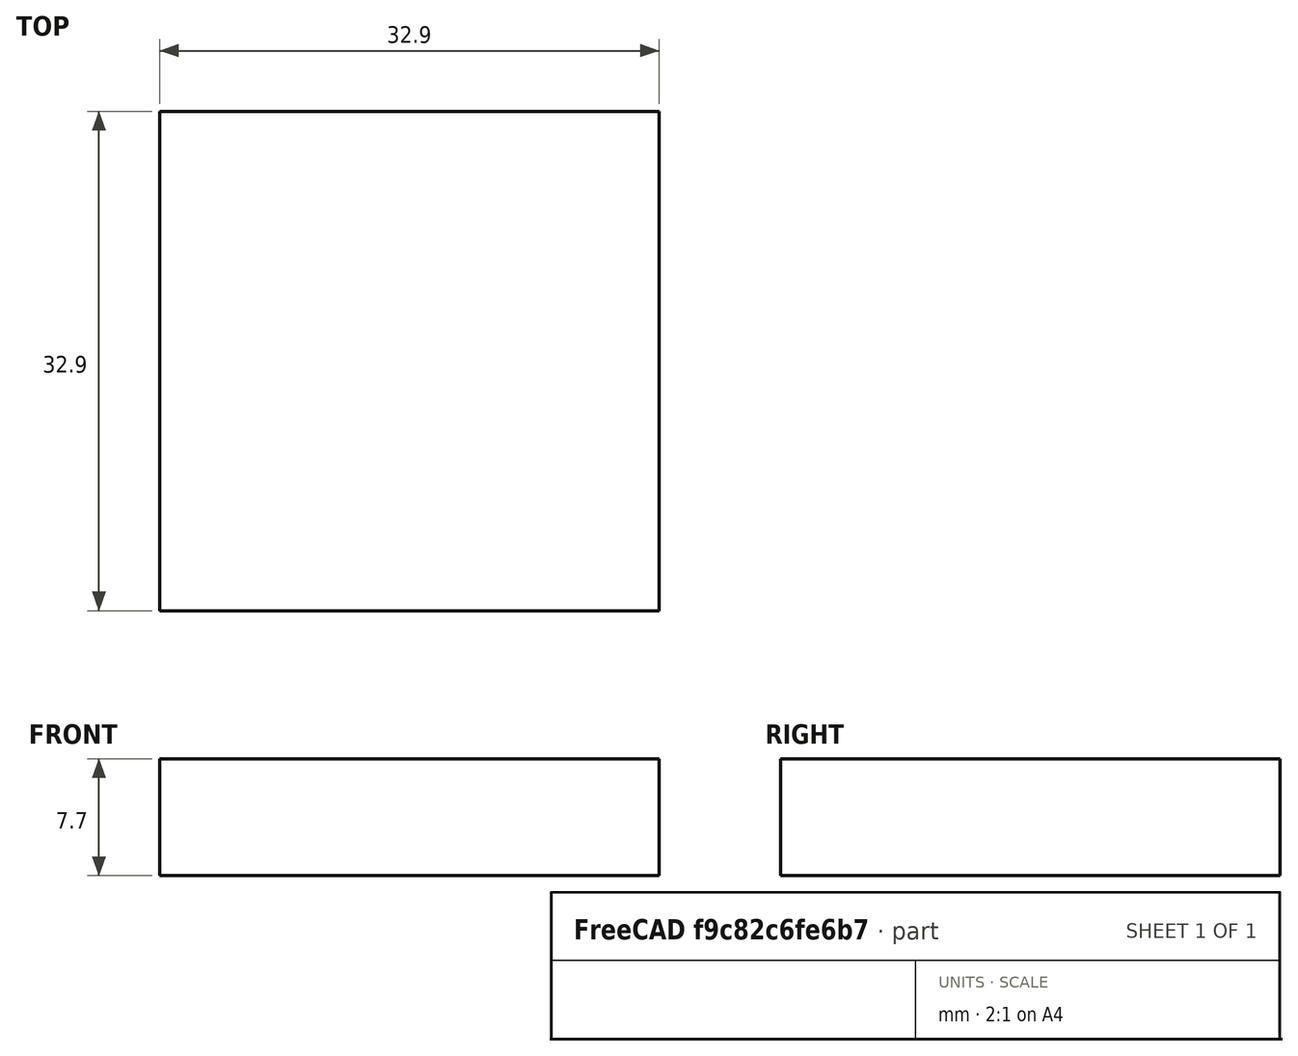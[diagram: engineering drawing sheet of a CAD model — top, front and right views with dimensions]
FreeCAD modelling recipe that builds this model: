
FCSTD DOCUMENT  (FreeCAD 0.18.4R)
Label: midi_pad
License: All rights reserved
LicenseURL: http://en.wikipedia.org/wiki/All_rights_reserved
objects: Path::FeaturePython×5, App::MeasureDistance×4, Sketcher::SketchObject×3, PartDesign::Pocket×2, Part::FeaturePython×2, PartDesign::Pad×1, Spreadsheet::Sheet×1, PartDesign::Body×1, App::FeaturePython×1, App::DocumentObjectGroup×1, Path::FeatureCompoundPython×1, Mesh::FeaturePython×1, Image::ImagePlane×1
note: 14 computed .brp shape members not serialized (recipe doc carries the construction recipe); baked Part::Feature solids carry a one-line shape summary decoded from their .brp

FEATURE [Sketcher::SketchObject] Sketch  label="circle"
  MapMode = 5
  Support = -> [XY_Plane]
  expr: Constraints[1] = parameters.balero_R + parameters.wall_thickness * 2
  sketch-geometry (1):
    g0: Circle CenterX=0 CenterY=0 CenterZ=0 NormalX=0 NormalY=0 NormalZ=1 AngleXU=0 Radius=11.45
  constraints (2):
    c: Coincident(g0,g-1)
    c: Diameter(g0) = 22.9
FEATURE [PartDesign::Pad] Pad  label="cilinder"
  Length = 7.7
  Length2 = 100
  Profile = -> Sketch
  Type = 0
  expr: Length = parameters.balero_h + parameters.cutout_d + parameters.separator
FEATURE [Sketcher::SketchObject] Sketch002  label="cutout"
  MapMode = 5
  Placement = pos=(0,0,0) rot=(1,0,0;3.14159rad)
  expr: Constraints[34] = (parameters.balero_R + parameters.wall_thickness) / 2
  expr: Constraints[33] = (parameters.balero_R + parameters.wall_thickness) / 2
  expr: Constraints[32] = (parameters.balero_R + parameters.wall_thickness) / 2
  expr: Constraints[35] = (parameters.balero_R + parameters.wall_thickness) / 2
  expr: Constraints.pin_width = parameters.pin_w
  expr: Constraints[13] = parameters.r_w
  sketch-geometry (12):
    g0: LineSegment StartX=-9.7 StartY=5.1 StartZ=0 EndX=-5 EndY=5.1 EndZ=0
    g1: LineSegment StartX=-5 StartY=5.1 StartZ=0 EndX=-5 EndY=9.7 EndZ=0
    g2: LineSegment StartX=-5 StartY=9.7 StartZ=0 EndX=5 EndY=9.7 EndZ=0
    g3: LineSegment StartX=5 StartY=9.7 StartZ=0 EndX=5 EndY=5.1 EndZ=0
    g4: LineSegment StartX=5 StartY=5.1 StartZ=0 EndX=9.7 EndY=5.1 EndZ=0
    g5: LineSegment StartX=9.7 StartY=5.1 StartZ=0 EndX=9.7 EndY=-5.1 EndZ=0
    g6: LineSegment StartX=9.7 StartY=-5.1 StartZ=0 EndX=5 EndY=-5.1 EndZ=0
    g7: LineSegment StartX=5 StartY=-5.1 StartZ=0 EndX=5 EndY=-9.7 EndZ=0
    g8: LineSegment StartX=5 StartY=-9.7 StartZ=0 EndX=-5 EndY=-9.7 EndZ=0
    g9: LineSegment StartX=-5 StartY=-9.7 StartZ=0 EndX=-5 EndY=-5.1 EndZ=0
    g10: LineSegment StartX=-5 StartY=-5.1 StartZ=0 EndX=-9.7 EndY=-5.1 EndZ=0
    g11: LineSegment StartX=-9.7 StartY=-5.1 StartZ=0 EndX=-9.7 EndY=5.1 EndZ=0
  constraints (36):
    c: Horizontal(g0)
    c: Coincident(g0,g1)
    c: Coincident(g1,g2)
    c: Coincident(g2,g3)
    c: Coincident(g3,g4)
    c: Coincident(g4,g5)
    c: Coincident(g5,g6)
    c: Coincident(g6,g7)
    c: Coincident(g7,g8)
    c: Coincident(g8,g9)
    c: Coincident(g9,g10)
    c: Coincident(g10,g11)
    c: Coincident(g11,g0)
    c: DistanceX(g2,g2) = 10
    c: Equal(g2,g8)
    c: Vertical(g1)
    c: Vertical(g3)
    c: Vertical(g5)
    c: Vertical(g11)
    c: Vertical(g9)
    c: Horizontal(g2)
    c: Horizontal(g4)
    c: Horizontal(g6)
    c: Horizontal(g8)
    c: DistanceY(g5,g5) = 10.2  'pin_width'
    c: Equal(g5,g11)
    c: Equal(g1,g3)
    c: Equal(g4,g6)
    c: Equal(g9,g7)
    c: Equal(g10,g0)
    c: Equal(g0,g4)
    c: Equal(g9,g1)
    c: DistanceX(g-1,g4) = 9.7
    c: DistanceX(g0,g-1) = 9.7
    c: DistanceY(g-1,g1) = 9.7
    c: DistanceY(g8,g-1) = 9.7
FEATURE [Spreadsheet::Sheet] Spreadsheet  label="parameters"
  cells = A1=balero_R; B1(balero_R)=15.9; A2=balero_r; B2(balero_r)=4.7; A3=balero_h; B3(balero_h)=5; A4=pin_w; B4(pin_w)=10.2; A5=r_w; B5(r_w)=10; A6=cutout_d; B6(cutout_d)=1.7; A7=wall_thickness; B7(wall_thickness)=3.5; A8=separator; B8(separator)=1
FEATURE [Sketcher::SketchObject] Sketch003  label="balero"
  MapMode = 5
  Placement = pos=(0,0,7.7) rot=(0,0,1;0rad)
  Support = -> [Pad]
  expr: Constraints[1] = parameters.balero_R
  sketch-geometry (1):
    g0: Circle CenterX=0 CenterY=0 CenterZ=0 NormalX=0 NormalY=0 NormalZ=1 AngleXU=0 Radius=7.95
  constraints (2):
    c: Coincident(g0,g-1)
    c: Diameter(g0) = 15.9
FEATURE [PartDesign::Pocket] Pocket  label="Pocket Balero"
  BaseFeature = -> Pad
  Length = 5
  Length2 = 100
  Profile = -> Sketch003
  Type = 0
  expr: Length = parameters.balero_h
FEATURE [PartDesign::Pocket] Pocket001  label="Pocket Cutout"
  BaseFeature = -> Pocket
  Length = 1.7
  Length2 = 100
  Profile = -> Sketch002
  Type = 0
  expr: Length = parameters.cutout_d
FEATURE [PartDesign::Body] Body
  Group = -> [Sketch,Pad,Sketch002,Sketch003,Pocket,Pocket001]
  Origin = -> Origin
  Tip = -> Pocket001
FEATURE [App::FeaturePython] SetupSheet  # Path/CAM operation (typed FeaturePython)
  ClearanceHeightExpression = OpStockZMax+SetupSheet.ClearanceHeightOffset
  ClearanceHeightOffset = 5
  FinalDepthExpression = OpFinalDepth
  HorizRapid = 0
  SafeHeightExpression = OpStockZMax+SetupSheet.SafeHeightOffset
  SafeHeightOffset = 3
  StartDepthExpression = OpStartDepth
  StepDownExpression = OpToolDiameter
  VertRapid = 0
FEATURE [Part::FeaturePython] Clone  label="Model-Body"  # Draft clone (typed FeaturePython)
  AttacherType = Attacher::AttachEngine3D
  Fuse = false
  Objects = -> [Body]
  PathResource = Model
  Scale = (1,1,1)
FEATURE [App::DocumentObjectGroup] Model
  Group = -> [Clone]
FEATURE [Part::FeaturePython] Stock001  label="Stock acrylic"  # WARN: FeaturePython — macro-defined, semantics opaque (R4)
  Base = -> Model
  ExtXneg = 5
  ExtXpos = 5
  ExtYneg = 5
  ExtYpos = 5
  ExtZneg = 0
  ExtZpos = 0
  Placement = pos=(-11.45,-11.45,0) rot=(0,0,1;0rad)
  StockType = FromBase
FEATURE [Path::FeaturePython] T2__Default_mill  label="mill standar"  # Path/CAM operation (typed FeaturePython)
  HorizFeed = 15
  HorizRapid = 0
  SpindleDir = 0
  SpindleSpeed = 12000
  ToolNumber = 1
  VertFeed = 15
  VertRapid = 0
  expr: HorizRapid = SetupSheet.HorizRapid
  expr: VertRapid = SetupSheet.VertRapid
FEATURE [Path::FeaturePython] Pocket_3D  label="Balero_Pocket_3D"  # Path/CAM operation (typed FeaturePython)
  Active = true
  AreaParams:
    Tolerance = 1e-07
    FitArcs = True
    Simplify = False
    CleanDistance = 0.0
    Accuracy = 0.01
    Unit = 1.0
    MinArcPoints = 4
    MaxArcPoints = 100
    ClipperScale = 10000000.0
    Fill = 0
    Coplanar = 0
    Reorient = True
    Outline = False
    Explode = False
    OpenMode = 0
    Deflection = 0.01
    SubjectFill = 0
    ClipFill = 0
    Offset = 0.0
    ExtraPass = 0
    Stepover = 0.0
    LastStepover = 0.0
    JoinType = 0
    EndType = 0
    MiterLimit = 2.0
    RoundPrecision = 0.0
    PocketMode = 4
    ToolRadius = 1.5
    PocketExtraOffset = 0.0
    PocketStepover = 0.6000000000000001
    PocketLastStepover = 0.0
    FromCenter = True
    Angle = 45.0
    AngleShift = 0.0
    Shift = 0.0
    Thicken = False
    SectionCount = -1
    Stepdown = 1.0
    SectionOffset = 0.0
    SectionTolerance = 1e-06
    SectionMode = 2
    Project = False
  Base = -> [Clone]
  ClearanceHeight = 12.7
  CutMode = 0
  ExtraOffset = 0
  FinalDepth = 2.7
  FinishDepth = 0
  KeepToolDown = false
  MinTravel = false
  OffsetPattern = 3
  OpFinalDepth = 2.7
  OpStartDepth = 7.7
  OpStockZMax = 7.7
  OpStockZMin = 0
  OpToolDiameter = 3
  PathParams = {'orientation': 1, 'feedrate': 15.0, 'feedrate_v': 15.0, 'verbose': True, 'resume_height': 10.7, 'retraction': 12.7, 'return_end': True, 'preamble': False}
  SafeHeight = 10.7
  StartAt = 0
  StartDepth = 7.7
  StartPoint = (0,0,0)
  StepDown = 0.6
  StepOver = 20
  ToolController = -> T2__Default_mill
  UseStartPoint = false
  ZigZagAngle = 45
  expr: ClearanceHeight = OpStockZMax + SetupSheet.ClearanceHeightOffset
  expr: SafeHeight = OpStockZMax + SetupSheet.SafeHeightOffset
  expr: StepDown = OpToolDiameter * 0.2
  expr: FinalDepth = OpFinalDepth
  expr: StartDepth = OpStartDepth
FEATURE [Path::FeaturePython] Contour  # Path/CAM operation (typed FeaturePython)
  Active = true
  AreaParams:
    Tolerance = 1e-07
    FitArcs = True
    Simplify = False
    CleanDistance = 0.0
    Accuracy = 0.01
    Unit = 1.0
    MinArcPoints = 4
    MaxArcPoints = 100
    ClipperScale = 10000000.0
    Fill = 0
    Coplanar = 2
    Reorient = True
    Outline = False
    Explode = False
    OpenMode = 0
    Deflection = 0.01
    SubjectFill = 0
    ClipFill = 0
    Offset = 1.5
    ExtraPass = 0
    Stepover = 0.0
    LastStepover = 0.0
    JoinType = 0
    EndType = 0
    MiterLimit = 2.0
    RoundPrecision = 0.0
    PocketMode = 0
    ToolRadius = 1.0
    PocketExtraOffset = 0.0
    PocketStepover = 0.0
    PocketLastStepover = 0.0
    FromCenter = False
    Angle = 45.0
    AngleShift = 0.0
    Shift = 0.0
    Thicken = False
    SectionCount = -1
    Stepdown = 1.0
    SectionOffset = 0.0
    SectionTolerance = 1e-06
    SectionMode = 2
    Project = False
  ClearanceHeight = 12.7
  Direction = 0
  FinalDepth = 0
  JoinType = 0
  MiterLimit = 0.1
  OffsetExtra = 0
  OpFinalDepth = 0
  OpStartDepth = 7.7
  OpStockZMax = 7.7
  OpStockZMin = 0
  OpToolDiameter = 3
  PathParams = {'orientation': 1, 'feedrate': 15.0, 'feedrate_v': 15.0, 'verbose': True, 'resume_height': 10.7, 'retraction': 12.7, 'return_end': True, 'preamble': False}
  SafeHeight = 10.7
  Side = 0
  StartDepth = 7.7
  StartPoint = (0,0,0)
  StepDown = 0.6
  ToolController = -> T2__Default_mill
  UseComp = true
  UseStartPoint = false
  expr: ClearanceHeight = OpStockZMax + SetupSheet.ClearanceHeightOffset
  expr: SafeHeight = OpStockZMax + SetupSheet.SafeHeightOffset
  expr: StepDown = OpToolDiameter * 0.2
  expr: FinalDepth = OpFinalDepth
  expr: StartDepth = OpStartDepth
FEATURE [Path::FeaturePython] TagDressup  # Path/CAM operation (typed FeaturePython)
  Angle = 90
  Base = -> Contour
  Height = 2
  Positions = (6) [(-4.48226,-12.1484,0),(-12.7619,-2.19243,0),(-8.27966,9.95592,0),(3.92095,12.341,0),(12.5812,3.06393,0),(8.50562,-9.76359,0)]
  Radius = 0
  SegmentationFactor = 50
  Width = 2
FEATURE [Path::FeatureCompoundPython] Operations  # Path/CAM operation (typed FeaturePython)
  Group = -> [Pocket_3D,TagDressup]
  UsePlacements = false
FEATURE [Path::FeaturePython] Job  # Path/CAM operation (typed FeaturePython)
  GeometryTolerance = 0.01
  Model = -> Model
  Operations = -> Operations
  PostProcessor = 5
  SetupSheet = -> SetupSheet
  Stock = -> Stock001
  ToolController = -> [T2__Default_mill]
FEATURE [Mesh::FeaturePython] CutMaterial  # WARN: FeaturePython — macro-defined, semantics opaque (R4)
FEATURE [Image::ImagePlane] ImagePlane
  Placement = pos=(99.4,-140.15,3) rot=(0,0,1;0rad)
  XSize = 222.326
  YSize = 305.698
FEATURE [App::MeasureDistance] Distance  label="Distance: left to center"
  Distance = 11.5
  P1 = (-11.5,0,0)
  P2 = (0,0,0)
FEATURE [App::MeasureDistance] Distance001  label="Distance: right to center"
  Distance = 11.5
  P1 = (11.5,0,0)
  P2 = (0,0,0)
FEATURE [App::MeasureDistance] Distance002  label="Distance: bottom to center"
  Distance = 7.58
  P1 = (0,-7.58,0)
  P2 = (0,0,0)
FEATURE [App::MeasureDistance] Distance003  label="Distance: up to center"
  Distance = 7.56
  P1 = (0,7.56,0)
  P2 = (0,0,0)
